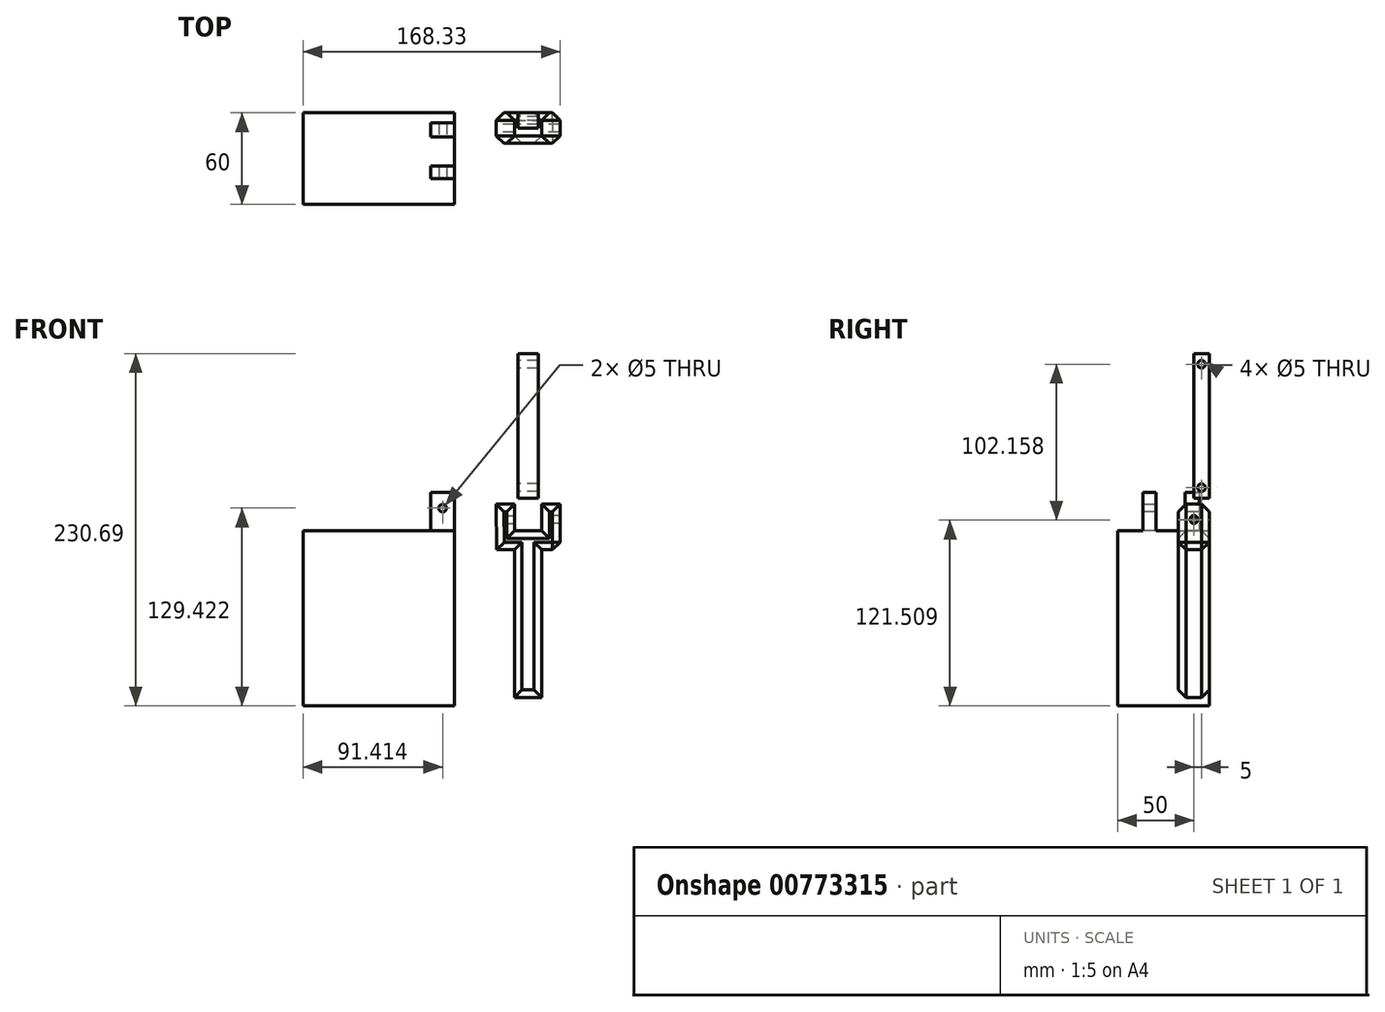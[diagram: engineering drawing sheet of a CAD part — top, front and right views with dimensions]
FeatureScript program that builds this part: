
annotation { "Feature Type Name" : "Feature", "Feature Type Description" : "" }
export const myFeature = defineFeature(function(context is Context, id is Id, definition is map)
    precondition{}
    {
        {
            var Q0;
            Q0=qCreatedBy(makeId("Front.planeOp"),FACE);
            var sketch = newSketch(context, id + "F0", { "sketchPlane" : qUnion([Q0])});
            skLineSegment(sketch, "E0", {"start": v(-12, 17.5) * mm, "end": v(0, 17.5) * mm});
            skLineSegment(sketch, "E1", {"start": v(0, 17.5) * mm, "end": v(0, 0) * mm});
            skLineSegment(sketch, "E2", {"start": v(0, 0) * mm, "end": v(17.92, 0) * mm});
            skLineSegment(sketch, "E3", {"start": v(17.92, 0) * mm, "end": v(17.92, 17.5) * mm});
            skLineSegment(sketch, "E4", {"start": v(17.92, 17.5) * mm, "end": v(29.92, 17.5) * mm});
            skLineSegment(sketch, "E5", {"start": v(29.92, 17.5) * mm, "end": v(29.92, -12.5) * mm});
            skLineSegment(sketch, "E6", {"start": v(29.92, -12.5) * mm, "end": v(17.92, -12.5) * mm});
            skLineSegment(sketch, "E7", {"start": v(17.92, -12.5) * mm, "end": v(17.92, -109.17) * mm});
            skLineSegment(sketch, "E8", {"start": v(17.92, -109.17) * mm, "end": v(0, -109.17) * mm});
            skLineSegment(sketch, "E9", {"start": v(0, -109.17) * mm, "end": v(0, -12.5) * mm});
            skLineSegment(sketch, "E10", {"start": v(0, -12.5) * mm, "end": v(-11.58, -12.5) * mm});
            skLineSegment(sketch, "E11", {"start": v(-12, 17.5) * mm, "end": v(-11.58, -12.5) * mm});
            skSolve(sketch);
        }
        {
            var Q0;
            Q0=makeQuery(id+"F0.imprint","IMPRINT",FACE,{"disambiguationData":[TD([[makeQuery(id+"F0.imprint","IMPRINT",EDGE,{"derivedFrom":sQuery(id+"F0.wireOp",EDGE,"E0")}),-1.0]])]});
            extrude(context, id + "F1", {"entities" : qUnion([Q0]), "depth" : 20 * mm, "offsetDistance" : 25 * mm});
        }
        {
            var Q0;
            Q0=makeQuery(id+"F1.opExtrude","CAP_FACE",FACE,{"disambiguationData":[OSD([sQuery(id+"F0.wireOp",EDGE,"E0"),sQuery(id+"F0.wireOp",EDGE,"E1"),sQuery(id+"F0.wireOp",EDGE,"E2"),sQuery(id+"F0.wireOp",EDGE,"E3"),sQuery(id+"F0.wireOp",EDGE,"E4"),sQuery(id+"F0.wireOp",EDGE,"E5"),sQuery(id+"F0.wireOp",EDGE,"E6"),sQuery(id+"F0.wireOp",EDGE,"E7"),sQuery(id+"F0.wireOp",EDGE,"E8"),sQuery(id+"F0.wireOp",EDGE,"E9"),sQuery(id+"F0.wireOp",EDGE,"E10"),sQuery(id+"F0.wireOp",EDGE,"E11")])],"isStart":true});
            var Q1;
            Q1=makeQuery(id+"F1.opExtrude","SWEPT_EDGE",EDGE,{"disambiguationData":[OSD([sQuery(id+"F0.wireOp",EDGE,"E5"),sQuery(id+"F0.wireOp",EDGE,"E6")])]});
            var Q2;
            Q2=makeQuery(id+"F1.opExtrude","CAP_FACE",FACE,{"disambiguationData":[OSD([sQuery(id+"F0.wireOp",EDGE,"E0"),sQuery(id+"F0.wireOp",EDGE,"E1"),sQuery(id+"F0.wireOp",EDGE,"E2"),sQuery(id+"F0.wireOp",EDGE,"E3"),sQuery(id+"F0.wireOp",EDGE,"E4"),sQuery(id+"F0.wireOp",EDGE,"E5"),sQuery(id+"F0.wireOp",EDGE,"E6"),sQuery(id+"F0.wireOp",EDGE,"E7"),sQuery(id+"F0.wireOp",EDGE,"E8"),sQuery(id+"F0.wireOp",EDGE,"E9"),sQuery(id+"F0.wireOp",EDGE,"E10"),sQuery(id+"F0.wireOp",EDGE,"E11")])],"isStart":false});
            chamfer(context, id + "F2", {"entities" : qUnion([Q0, Q1, Q2]), "width" : 5 * mm, "tangentPropagation" : true});
        }
        {
            var Q0;
            Q0=makeQuery(id+"F1.opExtrude","SWEPT_FACE",FACE,{"disambiguationData":[OSD([sQuery(id+"F0.wireOp",EDGE,"E11")])]});
            var sketch = newSketch(context, id + "F3", { "sketchPlane" : qUnion([Q0])});
            skPoint(sketch, "E12", {"position": v(10, 6.96) * mm});
            skPoint(sketch, "E12.positionSnap0", {"position": v(10, 17.66) * mm});
            skSolve(sketch);
        }
        {
            var Q0;
            Q0=sQuery(id+"F3.wireOp",VERTEX,"E12");
            var Q1;
            Q1=makeQuery(id+"F1.opExtrude","SWEPT_BODY",BODY,{"disambiguationData":[OSD([sQuery(id+"F0.wireOp",EDGE,"E0"),sQuery(id+"F0.wireOp",EDGE,"E1"),sQuery(id+"F0.wireOp",EDGE,"E2"),sQuery(id+"F0.wireOp",EDGE,"E3"),sQuery(id+"F0.wireOp",EDGE,"E4"),sQuery(id+"F0.wireOp",EDGE,"E5"),sQuery(id+"F0.wireOp",EDGE,"E6"),sQuery(id+"F0.wireOp",EDGE,"E7"),sQuery(id+"F0.wireOp",EDGE,"E8"),sQuery(id+"F0.wireOp",EDGE,"E9"),sQuery(id+"F0.wireOp",EDGE,"E10"),sQuery(id+"F0.wireOp",EDGE,"E11")])]});
            hole(context, id + "F4", {"style" : HoleStyle.SIMPLE, "endStyle" : HoleEndStyle.THROUGH, "holeDiameter" : 5 * mm, "majorDiameter" : 5 * mm, "isTappedThrough" : true, "tappedDepth" : 12 * mm, "tapClearance" : 3, "startFromSketch" : true, "locations" : qUnion([Q0]), "scope" : qUnion([Q1])});
        }
        {
            var Q0;
            Q0=qCreatedBy(makeId("Front.planeOp"),FACE);
            var sketch = newSketch(context, id + "F5", { "sketchPlane" : qUnion([Q0])});
            skLineSegment(sketch, "E13.bottom", {"start": v(2.3, 21.2) * mm, "end": v(15.76, 21.2) * mm});
            skLineSegment(sketch, "E13.top", {"start": v(2.3, 116.06) * mm, "end": v(15.76, 116.06) * mm});
            skLineSegment(sketch, "E13.left", {"start": v(2.3, 21.2) * mm, "end": v(2.3, 116.06) * mm});
            skLineSegment(sketch, "E13.right", {"start": v(15.76, 21.2) * mm, "end": v(15.76, 116.06) * mm});
            skSolve(sketch);
        }
        {
            var Q0;
            Q0=makeQuery(id+"F5.imprint","IMPRINT",FACE,{"disambiguationData":[TD([[makeQuery(id+"F5.imprint","IMPRINT",EDGE,{"derivedFrom":sQuery(id+"F5.wireOp",EDGE,"E13.bottom")}),1.0]])]});
            extrude(context, id + "F6", {"entities" : qUnion([Q0]), "depth" : 10 * mm, "offsetDistance" : 25 * mm});
        }
        {
            var Q0;
            Q0=makeQuery(id+"F6.opExtrude","SWEPT_FACE",FACE,{"disambiguationData":[OSD([sQuery(id+"F5.wireOp",EDGE,"E13.left")])]});
            var sketch = newSketch(context, id + "F7", { "sketchPlane" : qUnion([Q0])});
            skPoint(sketch, "E14", {"position": v(5, 109.04) * mm});
            skPoint(sketch, "E14.positionSnap0", {"position": v(5, 116.06) * mm});
            skPoint(sketch, "E15", {"position": v(5, 28.23) * mm});
            skPoint(sketch, "E15.positionSnap0", {"position": v(5, 21.2) * mm});
            skSolve(sketch);
        }
        {
            var Q0;
            Q0=sQuery(id+"F7.wireOp",VERTEX,"E14");
            var Q1;
            Q1=sQuery(id+"F7.wireOp",VERTEX,"E15");
            var Q2;
            Q2=makeQuery(id+"F6.opExtrude","SWEPT_BODY",BODY,{"disambiguationData":[OSD([sQuery(id+"F5.wireOp",EDGE,"E13.bottom"),sQuery(id+"F5.wireOp",EDGE,"E13.top"),sQuery(id+"F5.wireOp",EDGE,"E13.left"),sQuery(id+"F5.wireOp",EDGE,"E13.right")])]});
            hole(context, id + "F8", {"style" : HoleStyle.SIMPLE, "endStyle" : HoleEndStyle.THROUGH, "holeDiameter" : 5 * mm, "majorDiameter" : 5 * mm, "isTappedThrough" : true, "tappedDepth" : 12 * mm, "tapClearance" : 3, "startFromSketch" : true, "locations" : qUnion([Q0, Q1]), "scope" : qUnion([Q2])});
        }
        {
            var Q0;
            Q0=qCreatedBy(makeId("Front.planeOp"),FACE);
            var sketch = newSketch(context, id + "F9", { "sketchPlane" : qUnion([Q0])});
            skLineSegment(sketch, "E16.bottom", {"start": v(-138.4, 0) * mm, "end": v(-39.26, 0) * mm});
            skLineSegment(sketch, "E16.top", {"start": v(-138.4, -114.63) * mm, "end": v(-39.26, -114.63) * mm});
            skLineSegment(sketch, "E16.left", {"start": v(-138.4, 0) * mm, "end": v(-138.4, -114.63) * mm});
            skLineSegment(sketch, "E16.right", {"start": v(-39.26, 0) * mm, "end": v(-39.26, -114.63) * mm});
            skSolve(sketch);
        }
        {
            var Q0;
            Q0=makeQuery(id+"F9.imprint","IMPRINT",FACE,{"disambiguationData":[TD([[makeQuery(id+"F9.imprint","IMPRINT",EDGE,{"derivedFrom":sQuery(id+"F9.wireOp",EDGE,"E16.bottom")}),-1.0]])]});
            extrude(context, id + "F10", {"entities" : qUnion([Q0]), "depth" : 60 * mm, "offsetDistance" : 25 * mm});
        }
        {
            var Q0;
            Q0=makeQuery(id+"F10.opExtrude","SWEPT_FACE",FACE,{"disambiguationData":[OSD([sQuery(id+"F9.wireOp",EDGE,"E16.bottom")])]});
            var sketch = newSketch(context, id + "F11", { "sketchPlane" : qUnion([Q0])});
            skLineSegment(sketch, "E17.bottom", {"start": v(-39.26, -34.87) * mm, "end": v(-54.73, -34.87) * mm});
            skLineSegment(sketch, "E17.top", {"start": v(-39.26, -43.18) * mm, "end": v(-54.73, -43.18) * mm});
            skLineSegment(sketch, "E17.left", {"start": v(-39.26, -34.87) * mm, "end": v(-39.26, -43.18) * mm});
            skLineSegment(sketch, "E17.right", {"start": v(-54.73, -34.87) * mm, "end": v(-54.73, -43.18) * mm});
            skLineSegment(sketch, "E18.bottom", {"start": v(-54.73, -6.5) * mm, "end": v(-39.26, -6.5) * mm});
            skLineSegment(sketch, "E18.top", {"start": v(-54.73, -15.67) * mm, "end": v(-39.26, -15.67) * mm});
            skLineSegment(sketch, "E18.left", {"start": v(-54.73, -6.5) * mm, "end": v(-54.73, -15.67) * mm});
            skLineSegment(sketch, "E18.right", {"start": v(-39.26, -6.5) * mm, "end": v(-39.26, -15.67) * mm});
            skSolve(sketch);
        }
        {
            var Q0;
            Q0=makeQuery(id+"F11.imprint","IMPRINT",FACE,{"disambiguationData":[TD([[makeQuery(id+"F11.imprint","IMPRINT",EDGE,{"derivedFrom":sQuery(id+"F11.wireOp",EDGE,"E18.bottom")}),-1.0]])]});
            var Q1;
            Q1=makeQuery(id+"F11.imprint","IMPRINT",FACE,{"disambiguationData":[TD([[makeQuery(id+"F11.imprint","IMPRINT",EDGE,{"derivedFrom":sQuery(id+"F11.wireOp",EDGE,"E17.bottom")}),1.0]])]});
            extrude(context, id + "F12", {"entities" : qUnion([Q0, Q1]), "operationType" : NewBodyOperationType.ADD, "depth" : 25 * mm, "offsetDistance" : 25 * mm});
        }
        {
            var Q0;
            Q0=makeQuery(id+"F12.opExtrude","SWEPT_FACE",FACE,{"disambiguationData":[OSD([sQuery(id+"F11.wireOp",EDGE,"E17.top")])]});
            var sketch = newSketch(context, id + "F13", { "sketchPlane" : qUnion([Q0])});
            skPoint(sketch, "E19", {"position": v(-47, 14.8) * mm});
            skPoint(sketch, "E19.positionSnap0", {"position": v(-47, 25) * mm});
            skSolve(sketch);
        }
        {
            var Q0;
            Q0=sQuery(id+"F13.wireOp",VERTEX,"E19");
            var Q1;
            Q1=makeQuery(id+"F10.opExtrude","SWEPT_BODY",BODY,{"disambiguationData":[OSD([sQuery(id+"F9.wireOp",EDGE,"E16.bottom"),sQuery(id+"F9.wireOp",EDGE,"E16.top"),sQuery(id+"F9.wireOp",EDGE,"E16.left"),sQuery(id+"F9.wireOp",EDGE,"E16.right")])]});
            hole(context, id + "F14", {"style" : HoleStyle.SIMPLE, "endStyle" : HoleEndStyle.THROUGH, "holeDiameter" : 5 * mm, "majorDiameter" : 5 * mm, "isTappedThrough" : true, "tappedDepth" : 12 * mm, "tapClearance" : 3, "startFromSketch" : true, "locations" : qUnion([Q0]), "scope" : qUnion([Q1])});
        }
    });
